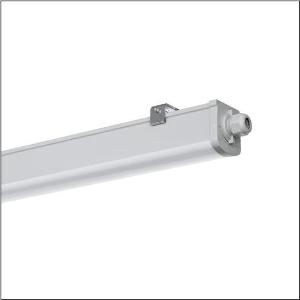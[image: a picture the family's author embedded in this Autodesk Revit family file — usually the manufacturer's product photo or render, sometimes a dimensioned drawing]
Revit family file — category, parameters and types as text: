
# Revit family: monsun_r__31_51fa20dp460b_68f5
name_source: partatom
category: Lighting Fixtures
units: mm (PartAtom-declared; Revit-internal decimal feet)

## family parameters
Cut with Voids When Loaded = No
Host = Face
Light Source = No
Part Type = Normal
Room Calculation Point = No
Round Connector Dimension = Use Diameter
Shared = No

## types (1)
- Monsun® 31 (1 x LED, 6700 lm, 50 W, 4000K)
    Apparent Load = 50 VA
    CIE Flux Codes = 42 72 91 92 100
    Color Rendering = 80
    Color Temperature = 4000K
    Default Elevation = 1800 mm
    Description = Monsun® 31, damp-proof luminaire, primary optical cover: diffuser, of PC, frosted, light emission: direct distribution, primary light characteristic: symmetric, installation type: surface-mounted, LED, rated luminous flux: 6.700lm, luminous efficacy: 134lm/W, light colour: 840, colour temperature: 4000K, control gear: ECG, with terminal, 5+1-pole, max. 2.5mm², through-wiring: 3x 2.5mm² + 3x 1.5mm², mains connection: 220..240V, AC, 50/60Hz, rated input power: 50W, housing, luminaire housing, of PC, light grey (RAL 7035), length: 1.458mm, width: 68mm, height: 76mm, protection rating (complete): IP66, insulation class (complete): insulation class II (safety insulation), certification: CE, ENEC, UKCA, protection symbol: D, impact resistance: IK08, permissible operating ambient temperature: -20..+40°C, corresponds to IFS (International Featured Standards) requirements for safety and quality in the food industry, contact your sales advisor before using the luminaires in applications with unclear chemical exposure, large temperature fluctuations or condensation-forming humidity, packaging unit: 1 piece
    Height = 77 mm
    Lamp = 1 x LED
    Lamp Light Flux = 6700 lm
    Lamp Power = 50 W
    Lamp count = 1
    Length = 1518 mm
    Luminous efficacy = 134 lm/W
    Manufacturer = Siteco
    ModVariant = No
    Model = 51FA20DP460B
    Mounting Place = Ceiling
    Mounting Type = Surface mounted
    Number of Poles = 1
    OnlyDefault = Yes
    Power Factor = 1
    Product Name = Monsun® 31
    Product group = damp-proof luminaire
    ProductGroupID = 301
    Protection Class = Protection class II
    Protection Degree = IP 66
    RLX_Detail_Level = 1
    RLX_Emergency_Light_Flux = 0 lm
    RLX_Emergency_Type = 0
    RLX_Emergency_Type_DB = No
    RlxData = <blob elided: 33021 chars, md5=df2fb1a9>
    Socket = socket
    Standby Power = 0 W
    System Light Flux = 6700 lm
    System Power = 50 W
    Type Comments = Product without accessories
    Type Image = l_1006174.jpg
    URL = http://relux.com
    VarID = ---
    Voltage = 0 V
    Weight = 0.00 kg
    Width = 69 mm

## geometry (parser evidence)
native form markers: Blend x4, Sweep x14
no freeform markers — native parametric forms only
